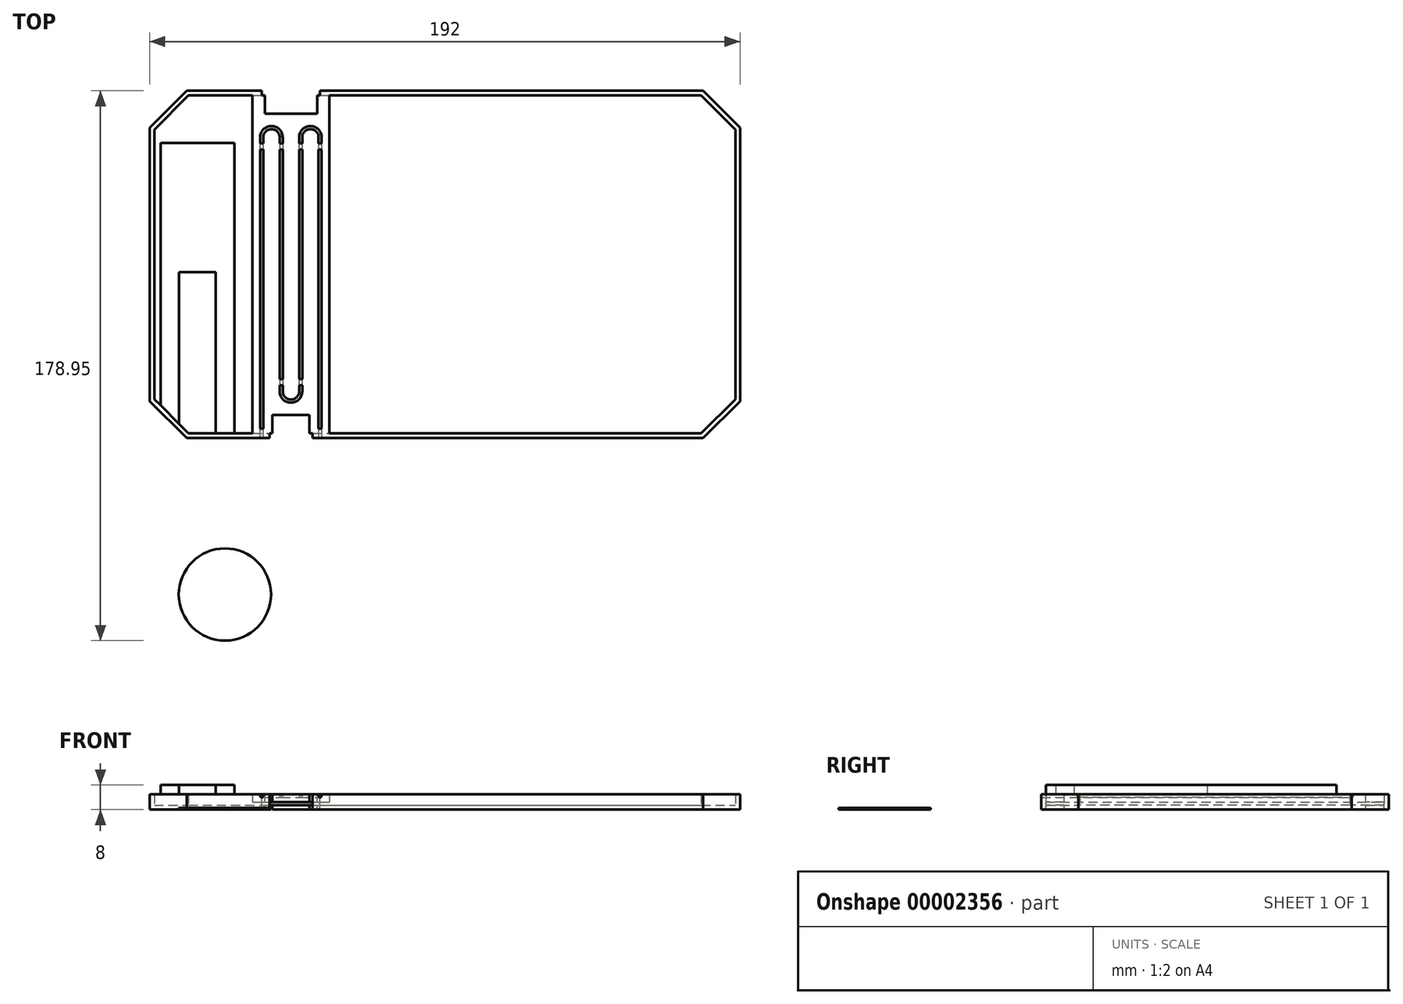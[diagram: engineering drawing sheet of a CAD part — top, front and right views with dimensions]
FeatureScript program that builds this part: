
annotation { "Feature Type Name" : "Feature", "Feature Type Description" : "" }
export const myFeature = defineFeature(function(context is Context, id is Id, definition is map)
    precondition{}
    {
        {
            var Q0;
            Q0=qCreatedBy(makeId("Top.planeOp"),FACE);
            var sketch = newSketch(context, id + "F0", { "sketchPlane" : qUnion([Q0])});
            skLineSegment(sketch, "E0.bottom", {"start": v(-84, 56.5) * mm, "end": v(84, 56.5) * mm});
            skLineSegment(sketch, "E0.top", {"start": v(-84, -56.5) * mm, "end": v(84, -56.5) * mm});
            skLineSegment(sketch, "E0.left", {"start": v(-96, 44.5) * mm, "end": v(-96, -44.5) * mm});
            skLineSegment(sketch, "E0.right", {"start": v(96, 44.5) * mm, "end": v(96, -44.5) * mm});
            skLineSegment(sketch, "E1", {"start": v(-96, 44.5) * mm, "end": v(-84, 56.5) * mm});
            skLineSegment(sketch, "E2", {"start": v(84, 56.5) * mm, "end": v(96, 44.5) * mm});
            skLineSegment(sketch, "E3", {"start": v(84, -56.5) * mm, "end": v(96, -44.5) * mm});
            skLineSegment(sketch, "E4", {"start": v(-84, -56.5) * mm, "end": v(-96, -44.5) * mm});
            skLineSegment(sketch, "E5", {"start": v(-90, 50.5) * mm, "end": v(90, -50.5) * mm, "construction": true});
            skLineSegment(sketch, "E6", {"start": v(90, 50.5) * mm, "end": v(-90, -50.5) * mm, "construction": true});
            skSolve(sketch);
        }
        {
            var Q0;
            Q0=makeQuery(id+"F0.imprint","IMPRINT",FACE,{"disambiguationData":[TD([[makeQuery(id+"F0.imprint","IMPRINT",EDGE,{"derivedFrom":sQuery(id+"F0.wireOp",EDGE,"E0.bottom")}),-1.0]])]});
            extrude(context, id + "F1", {"entities" : qUnion([Q0]), "depth" : 5 * mm});
        }
        {
            var Q0;
            Q0=makeQuery(id+"F1.opExtrude","CAP_FACE",FACE,{"disambiguationData":[OSD([sQuery(id+"F0.wireOp",EDGE,"E0.bottom"),sQuery(id+"F0.wireOp",EDGE,"E0.top"),sQuery(id+"F0.wireOp",EDGE,"E0.left"),sQuery(id+"F0.wireOp",EDGE,"E0.right"),sQuery(id+"F0.wireOp",EDGE,"E1"),sQuery(id+"F0.wireOp",EDGE,"E2"),sQuery(id+"F0.wireOp",EDGE,"E3"),sQuery(id+"F0.wireOp",EDGE,"E4")])],"isStart":false});
            shell(context, id + "F2", {"entities" : qUnion([Q0]), "thickness" : 1.5 * mm});
        }
        {
            var Q0;
            Q0=makeQuery(id+"F1.opExtrude","CAP_FACE",FACE,{"disambiguationData":[OSD([sQuery(id+"F0.wireOp",EDGE,"E0.bottom"),sQuery(id+"F0.wireOp",EDGE,"E0.top"),sQuery(id+"F0.wireOp",EDGE,"E0.left"),sQuery(id+"F0.wireOp",EDGE,"E0.right"),sQuery(id+"F0.wireOp",EDGE,"E1"),sQuery(id+"F0.wireOp",EDGE,"E2"),sQuery(id+"F0.wireOp",EDGE,"E3"),sQuery(id+"F0.wireOp",EDGE,"E4")])],"isStart":false});
            var sketch = newSketch(context, id + "F3", { "sketchPlane" : qUnion([Q0])});
            skLineSegment(sketch, "E7", {"start": v(-89.5, -56.5) * mm, "end": v(-89.5, 33.5) * mm, "construction": true});
            skArc(sketch, "E8", {"start": v(-83.5, 33.5) * mm, "mid": v(-86.5, 36.5) * mm, "end": v(-89.5, 33.5) * mm, "construction": true});
            skLineSegment(sketch, "E9", {"start": v(-83.5, 33.5) * mm, "end": v(-83.5, 3.5) * mm, "construction": true});
            skLineSegment(sketch, "E10", {"start": v(-77.5, 3.5) * mm, "end": v(-77.5, 33.5) * mm, "construction": true});
            skLineSegment(sketch, "E11", {"start": v(-71.5, 33.5) * mm, "end": v(-71.5, -56.5) * mm, "construction": true});
            skArc(sketch, "E12", {"start": v(-71.5, 33.5) * mm, "mid": v(-74.5, 36.5) * mm, "end": v(-77.5, 33.5) * mm, "construction": true});
            skArc(sketch, "E13", {"start": v(-83.5, 3.5) * mm, "mid": v(-80.5, 0.5) * mm, "end": v(-77.5, 3.5) * mm, "construction": true});
            skLineSegment(sketch, "E14", {"start": v(-92.5, -56.5) * mm, "end": v(-86.5, -56.5) * mm});
            skLineSegment(sketch, "E15", {"start": v(-68.5, -56.5) * mm, "end": v(-68.5, 39.5) * mm});
            skLineSegment(sketch, "E16", {"start": v(-68.5, 39.5) * mm, "end": v(-92.5, 39.5) * mm});
            skLineSegment(sketch, "E17", {"start": v(-92.5, 39.5) * mm, "end": v(-92.5, -56.5) * mm});
            skLineSegment(sketch, "E18", {"start": v(-86.5, -56.5) * mm, "end": v(-86.5, -2.5) * mm});
            skLineSegment(sketch, "E19", {"start": v(-86.5, -2.5) * mm, "end": v(-74.5, -2.5) * mm});
            skLineSegment(sketch, "E20", {"start": v(-74.5, -2.5) * mm, "end": v(-74.5, -56.5) * mm});
            skLineSegment(sketch, "E21.trimOffspring", {"start": v(-74.5, -56.5) * mm, "end": v(-68.5, -56.5) * mm});
            skSolve(sketch);
        }
        {
            var Q0;
            {var subQ13=sQuery(id+"F3.wireOp",EDGE,"E16");Q0=makeQuery(id+"F3.imprint","IMPRINT",FACE,{"disambiguationData":[TD([[makeQuery(id+"F3.imprint","IMPRINT",EDGE,{"derivedFrom":subQ13}),1.0]])]});}
            extrude(context, id + "F4", {"entities" : qUnion([Q0]), "depth" : 3 * mm});
        }
        {
            var Q0;
            Q0=makeQuery(id+"F1.opExtrude","CAP_FACE",FACE,{"disambiguationData":[OSD([sQuery(id+"F0.wireOp",EDGE,"E0.bottom"),sQuery(id+"F0.wireOp",EDGE,"E0.top"),sQuery(id+"F0.wireOp",EDGE,"E0.left"),sQuery(id+"F0.wireOp",EDGE,"E0.right"),sQuery(id+"F0.wireOp",EDGE,"E1"),sQuery(id+"F0.wireOp",EDGE,"E2"),sQuery(id+"F0.wireOp",EDGE,"E3"),sQuery(id+"F0.wireOp",EDGE,"E4")])],"isStart":false});
            var sketch = newSketch(context, id + "F5", { "sketchPlane" : qUnion([Q0])});
            skLineSegment(sketch, "E22.bottom", {"start": v(-62.58, -56.5) * mm, "end": v(-37.58, -56.5) * mm});
            skLineSegment(sketch, "E22.top", {"start": v(-62.58, 56.5) * mm, "end": v(-37.58, 56.5) * mm});
            skLineSegment(sketch, "E22.left", {"start": v(-62.58, -56.5) * mm, "end": v(-62.58, 56.5) * mm});
            skLineSegment(sketch, "E22.right", {"start": v(-37.58, -56.5) * mm, "end": v(-37.58, 56.5) * mm});
            skSolve(sketch);
        }
        {
            var Q0;
            Q0 = qSketchRegion(id + "F5", true);
            extrude(context, id + "F6", {"entities" : qUnion([Q0]), "oppositeDirection" : true, "depth" : 2.5 * mm});
        }
        {
            var Q0;
            Q0=makeQuery(id+"F6.opExtrude","CAP_FACE",FACE,{"disambiguationData":[OSD([sQuery(id+"F5.wireOp",EDGE,"E22.bottom"),sQuery(id+"F5.wireOp",EDGE,"E22.top"),sQuery(id+"F5.wireOp",EDGE,"E22.left"),sQuery(id+"F5.wireOp",EDGE,"E22.right")])],"isStart":true});
            var sketch = newSketch(context, id + "F7", { "sketchPlane" : qUnion([Q0])});
            skLineSegment(sketch, "E23", {"start": v(-59.58, -56.5) * mm, "end": v(-59.58, 41.33) * mm});
            skLineSegment(sketch, "E24", {"start": v(-40.58, 41.33) * mm, "end": v(-40.58, -56.5) * mm});
            skLineSegment(sketch, "E25", {"start": v(-53.24, 41.33) * mm, "end": v(-53.24, -41.33) * mm});
            skLineSegment(sketch, "E26", {"start": v(-53.24, -41.33) * mm, "end": v(-46.91, -41.33) * mm, "construction": true});
            skLineSegment(sketch, "E27", {"start": v(-46.91, -41.33) * mm, "end": v(-46.91, 41.33) * mm});
            skLineSegment(sketch, "E28", {"start": v(-59.58, 41.33) * mm, "end": v(-53.24, 41.33) * mm, "construction": true});
            skLineSegment(sketch, "E29", {"start": v(-46.91, 41.33) * mm, "end": v(-40.58, 41.33) * mm, "construction": true});
            skArc(sketch, "E30", {"start": v(-53.24, 41.33) * mm, "mid": v(-56.41, 44.5) * mm, "end": v(-59.58, 41.33) * mm});
            skArc(sketch, "E31", {"start": v(-40.58, 41.33) * mm, "mid": v(-43.74, 44.5) * mm, "end": v(-46.91, 41.33) * mm});
            skArc(sketch, "E32", {"start": v(-53.24, -41.33) * mm, "mid": v(-50.08, -44.5) * mm, "end": v(-46.91, -41.33) * mm});
            skLineSegment(sketch, "E33", {"start": v(-62.58, 41.33) * mm, "end": v(-59.58, 41.33) * mm, "construction": true});
            skLineSegment(sketch, "E34", {"start": v(-40.58, 41.33) * mm, "end": v(-37.58, 41.33) * mm, "construction": true});
            skSolve(sketch);
        }
        {
            var Q0;
            Q0=makeQuery(id+"F6.opExtrude","SWEPT_FACE",FACE,{"disambiguationData":[OSD([sQuery(id+"F5.wireOp",EDGE,"E22.bottom")])]});
            var sketch = newSketch(context, id + "F8", { "sketchPlane" : qUnion([Q0])});
            skLineSegment(sketch, "E35", {"start": v(-59.08, 5) * mm, "end": v(-59.08, 4) * mm});
            skLineSegment(sketch, "E36", {"start": v(-60.08, 5) * mm, "end": v(-59.08, 5) * mm});
            skLineSegment(sketch, "E37", {"start": v(-60.08, 5) * mm, "end": v(-60.08, 4) * mm});
            skLineSegment(sketch, "E38", {"start": v(-60.08, 4) * mm, "end": v(-59.08, 4) * mm});
            skSolve(sketch);
        }
        {
            var Q0;
            Q0=makeQuery(id+"F8.imprint","IMPRINT",FACE,{"disambiguationData":[TD([[makeQuery(id+"F8.imprint","IMPRINT",EDGE,{"derivedFrom":sQuery(id+"F8.wireOp",EDGE,"E35")}),-1.0]])]});
            var Q1;
            Q1=sQuery(id+"F7.wireOp",EDGE,"E23");
            var Q2;
            Q2=sQuery(id+"F7.wireOp",EDGE,"E30");
            var Q3;
            Q3=sQuery(id+"F7.wireOp",EDGE,"E25");
            var Q4;
            Q4=sQuery(id+"F7.wireOp",EDGE,"E32");
            var Q5;
            Q5=sQuery(id+"F7.wireOp",EDGE,"E27");
            var Q6;
            Q6=sQuery(id+"F7.wireOp",EDGE,"E31");
            var Q7;
            Q7=sQuery(id+"F7.wireOp",EDGE,"E24");
            sweep(context, id + "F9", {"operationType" : NewBodyOperationType.REMOVE, "profiles" : qUnion([Q0]), "path" : qUnion([Q1, Q2, Q3, Q4, Q5, Q6, Q7])});
        }
        {
            var Q0;
            Q0=qCreatedBy(makeId("Top.planeOp"),FACE);
            var sketch = newSketch(context, id + "F10", { "sketchPlane" : qUnion([Q0])});
            skCircle(sketch, "E39", {"center": v(-71.54, -107.45) * mm, "radius": 15 * mm});
            skSolve(sketch);
        }
        {
            var Q0;
            Q0 = qSketchRegion(id + "F10", true);
            extrude(context, id + "F11", {"entities" : qUnion([Q0]), "depth" : 0.5 * mm});
        }
        {
            var Q0;
            {var subQ0=sQuery(id+"F5.wireOp",EDGE,"E22.bottom");var subQ1=sQuery(id+"F8.wireOp",EDGE,"E35");Q0=makeQuery(id+"F9.boolean.opBoolean","SPLIT",FACE,{"disambiguationData":[TD([makeQuery(id+"F9.opSweep","SWEPT_FACE",FACE,{"disambiguationData":[OSD([sQuery(id+"F7.wireOp",EDGE,"E23"),subQ1])]})])],"derivedFrom":makeQuery(id+"F6.opExtrude","CAP_FACE",FACE,{"disambiguationData":[OSD([subQ0,sQuery(id+"F5.wireOp",EDGE,"E22.top"),sQuery(id+"F5.wireOp",EDGE,"E22.left"),sQuery(id+"F5.wireOp",EDGE,"E22.right")])],"isStart":true})});}
            var sketch = newSketch(context, id + "F12", { "sketchPlane" : qUnion([Q0])});
            skLineSegment(sketch, "E40.bottom", {"start": v(-59.08, -53.5) * mm, "end": v(-60.08, -53.5) * mm});
            skLineSegment(sketch, "E40.top", {"start": v(-59.08, -56.5) * mm, "end": v(-60.08, -56.5) * mm});
            skLineSegment(sketch, "E40.left", {"start": v(-59.08, -53.5) * mm, "end": v(-59.08, -56.5) * mm});
            skLineSegment(sketch, "E40.right", {"start": v(-60.08, -53.5) * mm, "end": v(-60.08, -56.5) * mm});
            skLineSegment(sketch, "E41.bottom", {"start": v(-41.08, -53.5) * mm, "end": v(-40.08, -53.5) * mm});
            skLineSegment(sketch, "E41.top", {"start": v(-41.08, -56.5) * mm, "end": v(-40.08, -56.5) * mm});
            skLineSegment(sketch, "E41.left", {"start": v(-41.08, -53.5) * mm, "end": v(-41.08, -56.5) * mm});
            skLineSegment(sketch, "E41.right", {"start": v(-40.08, -53.5) * mm, "end": v(-40.08, -56.5) * mm});
            skLineSegment(sketch, "E42.bottom", {"start": v(-60.08, 39.33) * mm, "end": v(-59.08, 39.33) * mm});
            skLineSegment(sketch, "E42.top", {"start": v(-60.08, 37.33) * mm, "end": v(-59.08, 37.33) * mm});
            skLineSegment(sketch, "E42.left", {"start": v(-60.08, 39.33) * mm, "end": v(-60.08, 37.33) * mm});
            skLineSegment(sketch, "E42.right", {"start": v(-59.08, 39.33) * mm, "end": v(-59.08, 37.33) * mm});
            skLineSegment(sketch, "E43.bottom", {"start": v(-53.74, 39.33) * mm, "end": v(-52.74, 39.33) * mm});
            skLineSegment(sketch, "E43.top", {"start": v(-53.74, 37.33) * mm, "end": v(-52.74, 37.33) * mm});
            skLineSegment(sketch, "E43.left", {"start": v(-53.74, 39.33) * mm, "end": v(-53.74, 37.33) * mm});
            skLineSegment(sketch, "E43.right", {"start": v(-52.74, 39.33) * mm, "end": v(-52.74, 37.33) * mm});
            skLineSegment(sketch, "E44.bottom", {"start": v(-47.41, 39.33) * mm, "end": v(-46.41, 39.33) * mm});
            skLineSegment(sketch, "E44.top", {"start": v(-47.41, 37.33) * mm, "end": v(-46.41, 37.33) * mm});
            skLineSegment(sketch, "E44.left", {"start": v(-47.41, 39.33) * mm, "end": v(-47.41, 37.33) * mm});
            skLineSegment(sketch, "E44.right", {"start": v(-46.41, 39.33) * mm, "end": v(-46.41, 37.33) * mm});
            skLineSegment(sketch, "E45.bottom", {"start": v(-41.08, 39.33) * mm, "end": v(-40.08, 39.33) * mm});
            skLineSegment(sketch, "E45.top", {"start": v(-41.08, 37.33) * mm, "end": v(-40.08, 37.33) * mm});
            skLineSegment(sketch, "E45.left", {"start": v(-41.08, 39.33) * mm, "end": v(-41.08, 37.33) * mm});
            skLineSegment(sketch, "E45.right", {"start": v(-40.08, 39.33) * mm, "end": v(-40.08, 37.33) * mm});
            skLineSegment(sketch, "E46.bottom", {"start": v(-53.74, -37.33) * mm, "end": v(-52.74, -37.33) * mm});
            skLineSegment(sketch, "E46.top", {"start": v(-53.74, -39.33) * mm, "end": v(-52.74, -39.33) * mm});
            skLineSegment(sketch, "E46.left", {"start": v(-53.74, -37.33) * mm, "end": v(-53.74, -39.33) * mm});
            skLineSegment(sketch, "E46.right", {"start": v(-52.74, -37.33) * mm, "end": v(-52.74, -39.33) * mm});
            skLineSegment(sketch, "E47.bottom", {"start": v(-46.41, -37.33) * mm, "end": v(-47.41, -37.33) * mm});
            skLineSegment(sketch, "E47.top", {"start": v(-46.41, -39.33) * mm, "end": v(-47.41, -39.33) * mm});
            skLineSegment(sketch, "E47.left", {"start": v(-46.41, -37.33) * mm, "end": v(-46.41, -39.33) * mm});
            skLineSegment(sketch, "E47.right", {"start": v(-47.41, -37.33) * mm, "end": v(-47.41, -39.33) * mm});
            skSolve(sketch);
        }
        {
            var Q0;
            Q0 = qSketchRegion(id + "F12", true);
            extrude(context, id + "F13", {"entities" : qUnion([Q0]), "operationType" : NewBodyOperationType.ADD, "oppositeDirection" : true, "depth" : 0.2 * mm});
        }
        {
            var Q0;
            Q0=makeQuery(id+"F9.boolean.opBoolean","COPY",EDGE,{"derivedFrom":makeQuery(id+"F9.opSweep","SWEPT_EDGE",EDGE,{"disambiguationData":[OSD([sQuery(id+"F7.wireOp",EDGE,"E24"),sQuery(id+"F8.wireOp",EDGE,"E37"),sQuery(id+"F8.wireOp",EDGE,"E38")])]})});
            var Q1;
            Q1=makeQuery(id+"F9.boolean.opBoolean","COPY",EDGE,{"derivedFrom":makeQuery(id+"F9.opSweep","SWEPT_EDGE",EDGE,{"disambiguationData":[OSD([sQuery(id+"F7.wireOp",EDGE,"E24"),sQuery(id+"F8.wireOp",EDGE,"E35"),sQuery(id+"F8.wireOp",EDGE,"E38")])]})});
            fillet(context, id + "F14", {"entities" : qUnion([Q0, Q1]), "radius" : 0.5 * mm, "tangentPropagation" : true, "allowEdgeOverflow" : false});
        }
        {
            var Q0;
            {var subQ0=sQuery(id+"F5.wireOp",EDGE,"E22.bottom");var subQ1=sQuery(id+"F5.wireOp",EDGE,"E22.top");var subQ2=sQuery(id+"F5.wireOp",EDGE,"E22.left");var subQ3=sQuery(id+"F5.wireOp",EDGE,"E22.right");var subQ4=makeQuery(id+"F6.opExtrude","CAP_FACE",FACE,{"disambiguationData":[OSD([subQ0,subQ1,subQ2,subQ3])],"isStart":true});var subQ6=sQuery(id+"F8.wireOp",EDGE,"E35");var subQ12=sQuery(id+"F7.wireOp",EDGE,"E23");Q0=makeQuery(id+"F13.boolean.opBoolean","MERGE",FACE,{"derivedFrom":[makeQuery(id+"F9.boolean.opBoolean","SPLIT",FACE,{"disambiguationData":[TD([makeQuery(id+"F9.opSweep","SWEPT_FACE",FACE,{"disambiguationData":[OSD([subQ12,subQ6])]})])],"derivedFrom":subQ4}),makeQuery(id+"F9.boolean.opBoolean","SPLIT",FACE,{"disambiguationData":[TD([makeQuery(id+"F6.opExtrude","SWEPT_FACE",FACE,{"disambiguationData":[OSD([subQ1])]})])],"derivedFrom":subQ4}),makeQuery(id+"F13.opExtrude","CAP_FACE",FACE,{"disambiguationData":[OSD([sQuery(id+"F12.wireOp",EDGE,"E40.bottom"),sQuery(id+"F12.wireOp",EDGE,"E40.top"),sQuery(id+"F12.wireOp",EDGE,"E40.left"),sQuery(id+"F12.wireOp",EDGE,"E40.right")])],"isStart":true}),makeQuery(id+"F13.opExtrude","CAP_FACE",FACE,{"disambiguationData":[OSD([sQuery(id+"F12.wireOp",EDGE,"E41.bottom"),sQuery(id+"F12.wireOp",EDGE,"E41.top"),sQuery(id+"F12.wireOp",EDGE,"E41.left"),sQuery(id+"F12.wireOp",EDGE,"E41.right")])],"isStart":true}),makeQuery(id+"F13.opExtrude","CAP_FACE",FACE,{"disambiguationData":[OSD([sQuery(id+"F12.wireOp",EDGE,"E42.bottom"),sQuery(id+"F12.wireOp",EDGE,"E42.top"),sQuery(id+"F12.wireOp",EDGE,"E42.left"),sQuery(id+"F12.wireOp",EDGE,"E42.right")])],"isStart":true}),makeQuery(id+"F13.opExtrude","CAP_FACE",FACE,{"disambiguationData":[OSD([sQuery(id+"F12.wireOp",EDGE,"E43.bottom"),sQuery(id+"F12.wireOp",EDGE,"E43.top"),sQuery(id+"F12.wireOp",EDGE,"E43.left"),sQuery(id+"F12.wireOp",EDGE,"E43.right")])],"isStart":true}),makeQuery(id+"F13.opExtrude","CAP_FACE",FACE,{"disambiguationData":[OSD([sQuery(id+"F12.wireOp",EDGE,"E44.bottom"),sQuery(id+"F12.wireOp",EDGE,"E44.top"),sQuery(id+"F12.wireOp",EDGE,"E44.left"),sQuery(id+"F12.wireOp",EDGE,"E44.right")])],"isStart":true}),makeQuery(id+"F13.opExtrude","CAP_FACE",FACE,{"disambiguationData":[OSD([sQuery(id+"F12.wireOp",EDGE,"E45.bottom"),sQuery(id+"F12.wireOp",EDGE,"E45.top"),sQuery(id+"F12.wireOp",EDGE,"E45.left"),sQuery(id+"F12.wireOp",EDGE,"E45.right")])],"isStart":true}),makeQuery(id+"F13.opExtrude","CAP_FACE",FACE,{"disambiguationData":[OSD([sQuery(id+"F12.wireOp",EDGE,"E46.bottom"),sQuery(id+"F12.wireOp",EDGE,"E46.top"),sQuery(id+"F12.wireOp",EDGE,"E46.left"),sQuery(id+"F12.wireOp",EDGE,"E46.right")])],"isStart":true}),makeQuery(id+"F13.opExtrude","CAP_FACE",FACE,{"disambiguationData":[OSD([sQuery(id+"F12.wireOp",EDGE,"E47.bottom"),sQuery(id+"F12.wireOp",EDGE,"E47.top"),sQuery(id+"F12.wireOp",EDGE,"E47.left"),sQuery(id+"F12.wireOp",EDGE,"E47.right")])],"isStart":true})]});}
            var sketch = newSketch(context, id + "F15", { "sketchPlane" : qUnion([Q0])});
            skLineSegment(sketch, "E48", {"start": v(-57.08, -56.5) * mm, "end": v(-57.08, -55) * mm});
            skLineSegment(sketch, "E49", {"start": v(-57.08, -55) * mm, "end": v(-56.08, -55) * mm});
            skLineSegment(sketch, "E50", {"start": v(-56.08, -55) * mm, "end": v(-56.08, -49) * mm});
            skLineSegment(sketch, "E51", {"start": v(-56.08, -49) * mm, "end": v(-44.08, -49) * mm});
            skLineSegment(sketch, "E52", {"start": v(-44.08, -49) * mm, "end": v(-44.08, -55) * mm});
            skLineSegment(sketch, "E53", {"start": v(-44.08, -55) * mm, "end": v(-43.08, -55) * mm});
            skLineSegment(sketch, "E54", {"start": v(-43.08, -55) * mm, "end": v(-43.08, -56.5) * mm});
            skLineSegment(sketch, "E55", {"start": v(-43.08, -56.5) * mm, "end": v(-57.08, -56.5) * mm});
            skLineSegment(sketch, "E56", {"start": v(-50.08, -49) * mm, "end": v(-50.08, -56.5) * mm, "construction": true});
            skLineSegment(sketch, "E57", {"start": v(-59.58, 56.5) * mm, "end": v(-59.58, 55) * mm});
            skLineSegment(sketch, "E58", {"start": v(-59.58, 55) * mm, "end": v(-58.58, 55) * mm});
            skLineSegment(sketch, "E59", {"start": v(-58.58, 55) * mm, "end": v(-58.58, 49) * mm});
            skLineSegment(sketch, "E60", {"start": v(-58.58, 49) * mm, "end": v(-41.58, 49) * mm});
            skLineSegment(sketch, "E61", {"start": v(-41.58, 49) * mm, "end": v(-41.58, 55) * mm});
            skLineSegment(sketch, "E62", {"start": v(-41.58, 55) * mm, "end": v(-40.58, 55) * mm});
            skLineSegment(sketch, "E63", {"start": v(-40.58, 55) * mm, "end": v(-40.58, 56.5) * mm});
            skLineSegment(sketch, "E64", {"start": v(-40.58, 56.5) * mm, "end": v(-59.58, 56.5) * mm});
            skLineSegment(sketch, "E65", {"start": v(-50.08, 49) * mm, "end": v(-50.08, 56.5) * mm, "construction": true});
            skSolve(sketch);
        }
        {
            var Q0;
            Q0 = qSketchRegion(id + "F15", true);
            extrude(context, id + "F16", {"entities" : qUnion([Q0]), "operationType" : NewBodyOperationType.REMOVE, "oppositeDirection" : true, "depth" : 10 * mm});
        }
    });
